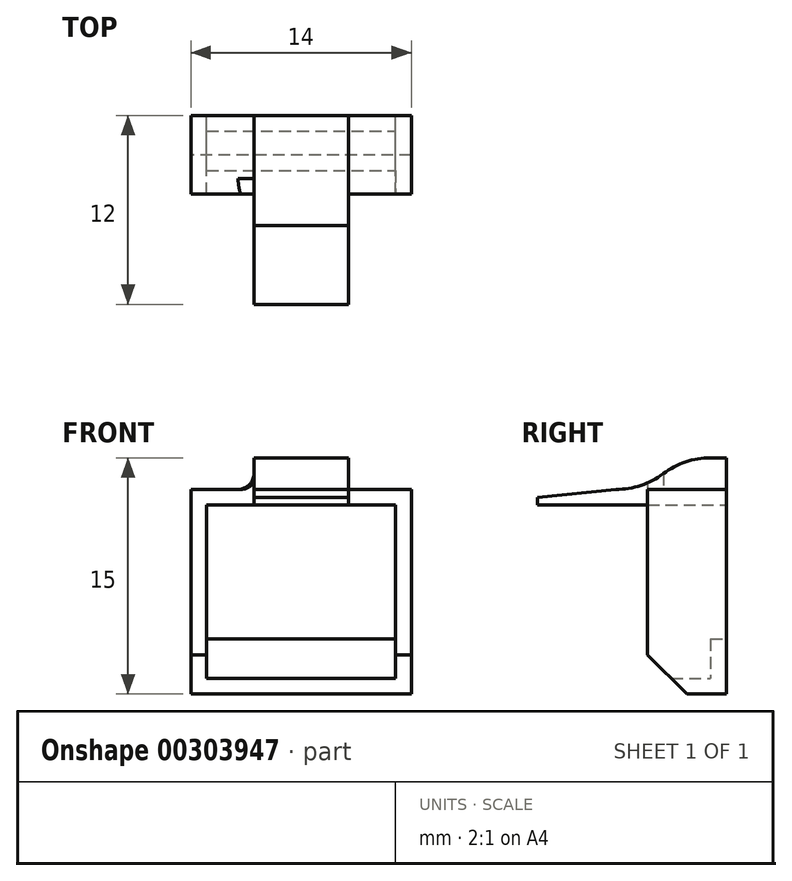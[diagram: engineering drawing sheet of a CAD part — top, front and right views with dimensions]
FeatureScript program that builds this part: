
annotation { "Feature Type Name" : "Feature", "Feature Type Description" : "" }
export const myFeature = defineFeature(function(context is Context, id is Id, definition is map)
    precondition{}
    {
        {
            var Q0;
            Q0=qCreatedBy(makeId("Front.planeOp"),FACE);
            var sketch = newSketch(context, id + "F0", { "sketchPlane" : qUnion([Q0])});
            skLineSegment(sketch, "E0.bottom", {"start": v(0, 0) * mm, "end": v(12, 0) * mm});
            skLineSegment(sketch, "E0.top", {"start": v(0, 11) * mm, "end": v(12, 11) * mm});
            skLineSegment(sketch, "E0.left", {"start": v(0, 0) * mm, "end": v(0, 11) * mm});
            skLineSegment(sketch, "E0.right", {"start": v(12, 0) * mm, "end": v(12, 11) * mm});
            skLineSegment(sketch, "E1.bottom", {"start": v(-1, -1) * mm, "end": v(13, -1) * mm});
            skLineSegment(sketch, "E1.top", {"start": v(-1, 12) * mm, "end": v(13, 12) * mm});
            skLineSegment(sketch, "E1.left", {"start": v(-1, -1) * mm, "end": v(-1, 12) * mm});
            skLineSegment(sketch, "E1.right", {"start": v(13, -1) * mm, "end": v(13, 12) * mm});
            skSolve(sketch);
        }
        {
            var Q0;
            Q0=makeQuery(id+"F0.imprint","IMPRINT",FACE,{"disambiguationData":[TD([[makeQuery(id+"F0.imprint","IMPRINT",EDGE,{"derivedFrom":sQuery(id+"F0.wireOp",EDGE,"E0.bottom")}),-1.0]])]});
            extrude(context, id + "F1", {"entities" : qUnion([Q0]), "depth" : 5 * mm});
        }
        {
            var Q0;
            Q0=makeQuery(id+"F1.opExtrude","CAP_FACE",FACE,{"disambiguationData":[OSD([sQuery(id+"F0.wireOp",EDGE,"E0.bottom"),sQuery(id+"F0.wireOp",EDGE,"E0.top"),sQuery(id+"F0.wireOp",EDGE,"E0.left"),sQuery(id+"F0.wireOp",EDGE,"E0.right"),sQuery(id+"F0.wireOp",EDGE,"E1.bottom"),sQuery(id+"F0.wireOp",EDGE,"E1.top"),sQuery(id+"F0.wireOp",EDGE,"E1.left"),sQuery(id+"F0.wireOp",EDGE,"E1.right")])],"isStart":false});
            var sketch = newSketch(context, id + "F2", { "sketchPlane" : qUnion([Q0])});
            skLineSegment(sketch, "E2.bottom", {"start": v(3, 11) * mm, "end": v(9, 11) * mm});
            skLineSegment(sketch, "E2.top", {"start": v(3, 12) * mm, "end": v(9, 12) * mm});
            skLineSegment(sketch, "E2.left", {"start": v(3, 11) * mm, "end": v(3, 12) * mm});
            skLineSegment(sketch, "E2.right", {"start": v(9, 11) * mm, "end": v(9, 12) * mm});
            skSolve(sketch);
        }
        {
            var Q0;
            Q0=makeQuery(id+"F2.imprint","IMPRINT",FACE,{"disambiguationData":[TD([[makeQuery(id+"F2.imprint","IMPRINT",EDGE,{"derivedFrom":sQuery(id+"F2.wireOp",EDGE,"E2.bottom")}),1.0]])]});
            extrude(context, id + "F3", {"entities" : qUnion([Q0]), "operationType" : NewBodyOperationType.ADD, "depth" : 7 * mm});
        }
        {
            var Q0;
            Q0=makeQuery(id+"F3.boolean.opBoolean","MERGE",FACE,{"derivedFrom":[makeQuery(id+"F1.opExtrude","SWEPT_FACE",FACE,{"disambiguationData":[OSD([sQuery(id+"F0.wireOp",EDGE,"E1.top")])]}),makeQuery(id+"F3.opExtrude","SWEPT_FACE",FACE,{"disambiguationData":[OSD([sQuery(id+"F2.wireOp",EDGE,"E2.top")])]})]});
            var sketch = newSketch(context, id + "F4", { "sketchPlane" : qUnion([Q0])});
            skLineSegment(sketch, "E3.bottom", {"start": v(9, -5) * mm, "end": v(3, -5) * mm});
            skLineSegment(sketch, "E3.top", {"start": v(9, 0) * mm, "end": v(3, 0) * mm});
            skLineSegment(sketch, "E3.left", {"start": v(9, -5) * mm, "end": v(9, 0) * mm});
            skLineSegment(sketch, "E3.right", {"start": v(3, -5) * mm, "end": v(3, 0) * mm});
            skSolve(sketch);
        }
        {
            var Q0;
            Q0=makeQuery(id+"F4.imprint","IMPRINT",FACE,{"disambiguationData":[TD([[makeQuery(id+"F4.imprint","IMPRINT",EDGE,{"derivedFrom":sQuery(id+"F4.wireOp",EDGE,"E3.bottom")}),-1.0]])]});
            extrude(context, id + "F5", {"entities" : qUnion([Q0]), "operationType" : NewBodyOperationType.ADD, "depth" : 2 * mm});
        }
        {
            var Q0;
            Q0=makeQuery(id+"F3.opExtrude","CAP_EDGE",EDGE,{"disambiguationData":[OSD([sQuery(id+"F2.wireOp",EDGE,"E2.top")])],"isStart":false});
            chamfer(context, id + "F6", {"entities" : qUnion([Q0]), "chamferType" : ChamferType.TWO_OFFSETS, "width1" : 5 * mm, "oppositeDirection" : false, "width2" : 0.5 * mm, "tangentPropagation" : true});
        }
        {
            var Q0;
            Q0=makeQuery(id+"F5.opExtrude","CAP_EDGE",EDGE,{"disambiguationData":[OSD([sQuery(id+"F4.wireOp",EDGE,"E3.bottom")])],"isStart":false});
            fillet(context, id + "F7", {"entities" : qUnion([Q0]), "radius" : 5 * mm, "tangentPropagation" : true, "allowEdgeOverflow" : false});
        }
        {
            var Q0;
            Q0=makeQuery(id+"F1.opExtrude","SWEPT_FACE",FACE,{"disambiguationData":[OSD([sQuery(id+"F0.wireOp",EDGE,"E0.bottom")])]});
            var sketch = newSketch(context, id + "F8", { "sketchPlane" : qUnion([Q0])});
            skLineSegment(sketch, "E4.bottom", {"start": v(0, 0) * mm, "end": v(12, 0) * mm});
            skLineSegment(sketch, "E4.top", {"start": v(0, -1) * mm, "end": v(12, -1) * mm});
            skLineSegment(sketch, "E4.left", {"start": v(0, 0) * mm, "end": v(0, -1) * mm});
            skLineSegment(sketch, "E4.right", {"start": v(12, 0) * mm, "end": v(12, -1) * mm});
            skSolve(sketch);
        }
        {
            var Q0;
            Q0=makeQuery(id+"F8.imprint","IMPRINT",FACE,{"disambiguationData":[TD([[makeQuery(id+"F8.imprint","IMPRINT",EDGE,{"derivedFrom":sQuery(id+"F8.wireOp",EDGE,"E4.bottom")}),-1.0]])]});
            extrude(context, id + "F9", {"entities" : qUnion([Q0]), "operationType" : NewBodyOperationType.ADD, "depth" : 2.5 * mm});
        }
        {
            var Q0;
            {var subQ0=sQuery(id+"F2.wireOp",EDGE,"E2.top");var subQ1=makeQuery(id+"F3.opExtrude","SWEPT_FACE",FACE,{"disambiguationData":[OSD([subQ0])]});var subQ2=sQuery(id+"F2.wireOp",EDGE,"E2.right");var subQ3=sQuery(id+"F2.wireOp",EDGE,"E2.left");var subQ4=sQuery(id+"F0.wireOp",EDGE,"E1.top");var subQ5=makeQuery(id+"F1.opExtrude","SWEPT_FACE",FACE,{"disambiguationData":[OSD([subQ4])]});var subQ6=sQuery(id+"F4.wireOp",EDGE,"E3.bottom");Q0=makeQuery(id+"F7.opFillet","BLEND_EDGE",EDGE,{"blendedFrom":[makeQuery(id+"F5.opExtrude","CAP_EDGE",EDGE,{"disambiguationData":[OSD([subQ6])],"isStart":false}),makeQuery(id+"F5.boolean.opBoolean","SPLIT",FACE,{"disambiguationData":[TD([makeQuery(id+"F3.opExtrude","CAP_FACE",FACE,{"disambiguationData":[OSD([sQuery(id+"F2.wireOp",EDGE,"E2.bottom"),subQ0,subQ3,subQ2])],"isStart":false})])],"derivedFrom":makeQuery(id+"F3.boolean.opBoolean","MERGE",FACE,{"derivedFrom":[subQ5,subQ1]})})],"blendedInto":[makeQuery(id+"F5.boolean.opBoolean","SPLIT",FACE,{"disambiguationData":[TD([makeQuery(id+"F3.opExtrude","CAP_FACE",FACE,{"disambiguationData":[OSD([sQuery(id+"F2.wireOp",EDGE,"E2.bottom"),subQ0,subQ3,subQ2])],"isStart":false})])],"derivedFrom":makeQuery(id+"F3.boolean.opBoolean","MERGE",FACE,{"derivedFrom":[subQ5,subQ1]})})]});}
            fillet(context, id + "F10", {"entities" : qUnion([Q0]), "radius" : 5 * mm, "tangentPropagation" : true, "allowEdgeOverflow" : false});
        }
        {
            var Q0;
            Q0=makeQuery(id+"F3.opExtrude","CAP_EDGE",EDGE,{"disambiguationData":[OSD([sQuery(id+"F2.wireOp",EDGE,"E2.right")])],"isStart":true});
            var Q1;
            Q1=makeQuery(id+"F3.opExtrude","CAP_EDGE",EDGE,{"disambiguationData":[OSD([sQuery(id+"F2.wireOp",EDGE,"E2.left")])],"isStart":true});
            var Q2;
            Q2=makeQuery(id+"F5.opExtrude","CAP_EDGE",EDGE,{"disambiguationData":[OSD([sQuery(id+"F4.wireOp",EDGE,"E3.left")])],"isStart":true});
            var Q3;
            Q3=makeQuery(id+"F5.opExtrude","CAP_EDGE",EDGE,{"disambiguationData":[OSD([sQuery(id+"F4.wireOp",EDGE,"E3.right")])],"isStart":true});
            fillet(context, id + "F11", {"entities" : qUnion([Q0, Q1, Q2, Q3]), "radius" : 1 * mm, "tangentPropagation" : true, "allowEdgeOverflow" : false});
        }
        {
            var Q0;
            Q0=makeQuery(id+"F1.opExtrude","CAP_EDGE",EDGE,{"disambiguationData":[OSD([sQuery(id+"F0.wireOp",EDGE,"E1.bottom")])],"isStart":false});
            chamfer(context, id + "F12", {"entities" : qUnion([Q0]), "width" : 2.5 * mm, "tangentPropagation" : true});
        }
    });
